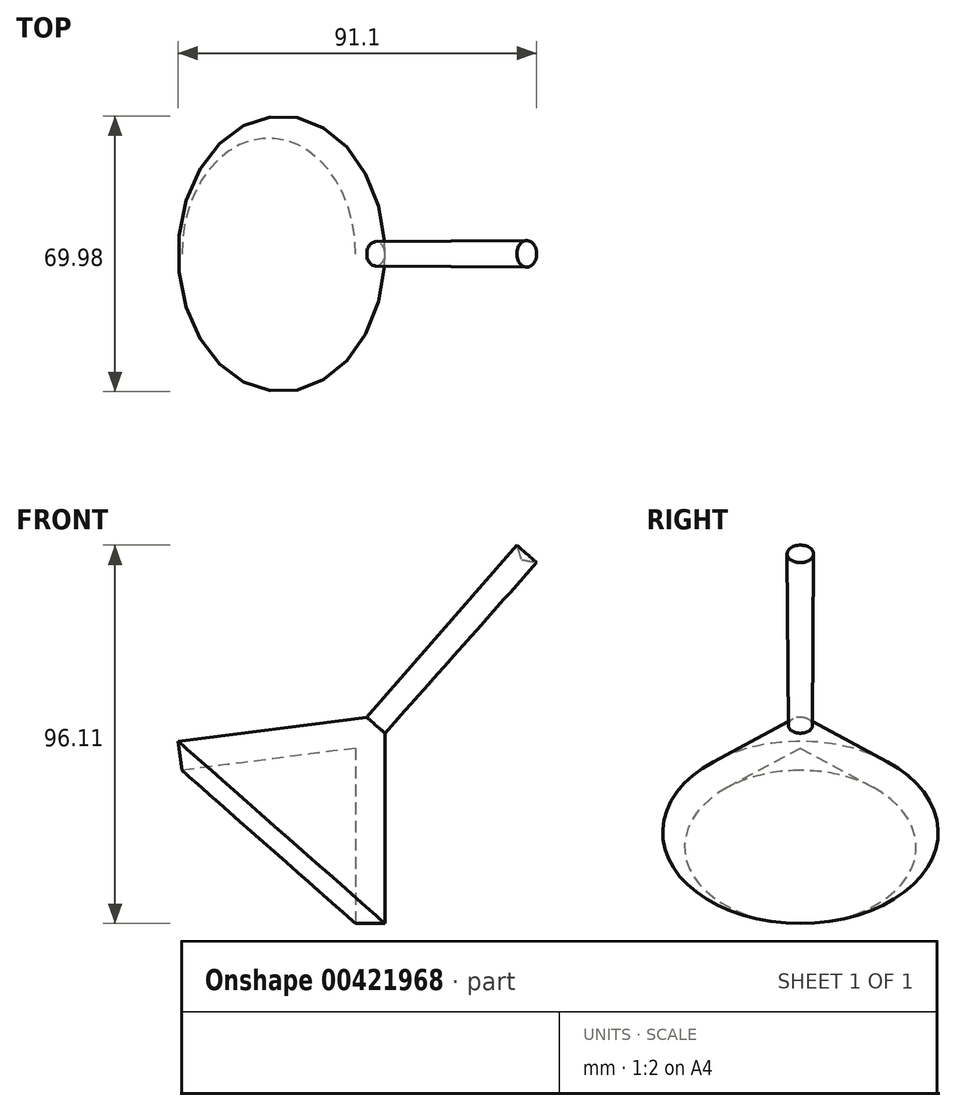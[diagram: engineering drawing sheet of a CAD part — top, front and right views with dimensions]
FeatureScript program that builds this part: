
annotation { "Feature Type Name" : "Feature", "Feature Type Description" : "" }
export const myFeature = defineFeature(function(context is Context, id is Id, definition is map)
    precondition{}
    {
        {
            var Q0;
            Q0=qCreatedBy(makeId("Front.planeOp"),FACE);
            var sketch = newSketch(context, id + "F0", { "sketchPlane" : qUnion([Q0])});
            skLineSegment(sketch, "E0", {"start": v(42.2, 47.93) * mm, "end": v(0, 0) * mm});
            skLineSegment(sketch, "E1", {"start": v(0, 0) * mm, "end": v(0, -44.5) * mm});
            skLineSegment(sketch, "E2", {"start": v(0, -44.5) * mm, "end": v(7.45, -44.5) * mm});
            skLineSegment(sketch, "E3", {"start": v(7.45, -44.5) * mm, "end": v(7.45, 3.82) * mm});
            skLineSegment(sketch, "E4", {"start": v(7.45, 3.82) * mm, "end": v(46.02, 47.17) * mm});
            skLineSegment(sketch, "E5", {"start": v(46.02, 47.17) * mm, "end": v(42.2, 47.93) * mm});
            skSolve(sketch);
        }
        {
            var Q0;
            Q0=makeQuery(id+"F0.imprint","IMPRINT",FACE,{"disambiguationData":[TD([[makeQuery(id+"F0.imprint","IMPRINT",EDGE,{"derivedFrom":sQuery(id+"F0.wireOp",EDGE,"E0")}),1.0]])]});
            var Q1;
            Q1=sQuery(id+"F0.wireOp",EDGE,"E0");
            revolve(context, id + "F1", {"entities" : qUnion([Q0]), "axis" : qUnion([Q1]), "revolveType" : RevolveType.FULL});
        }
    });
